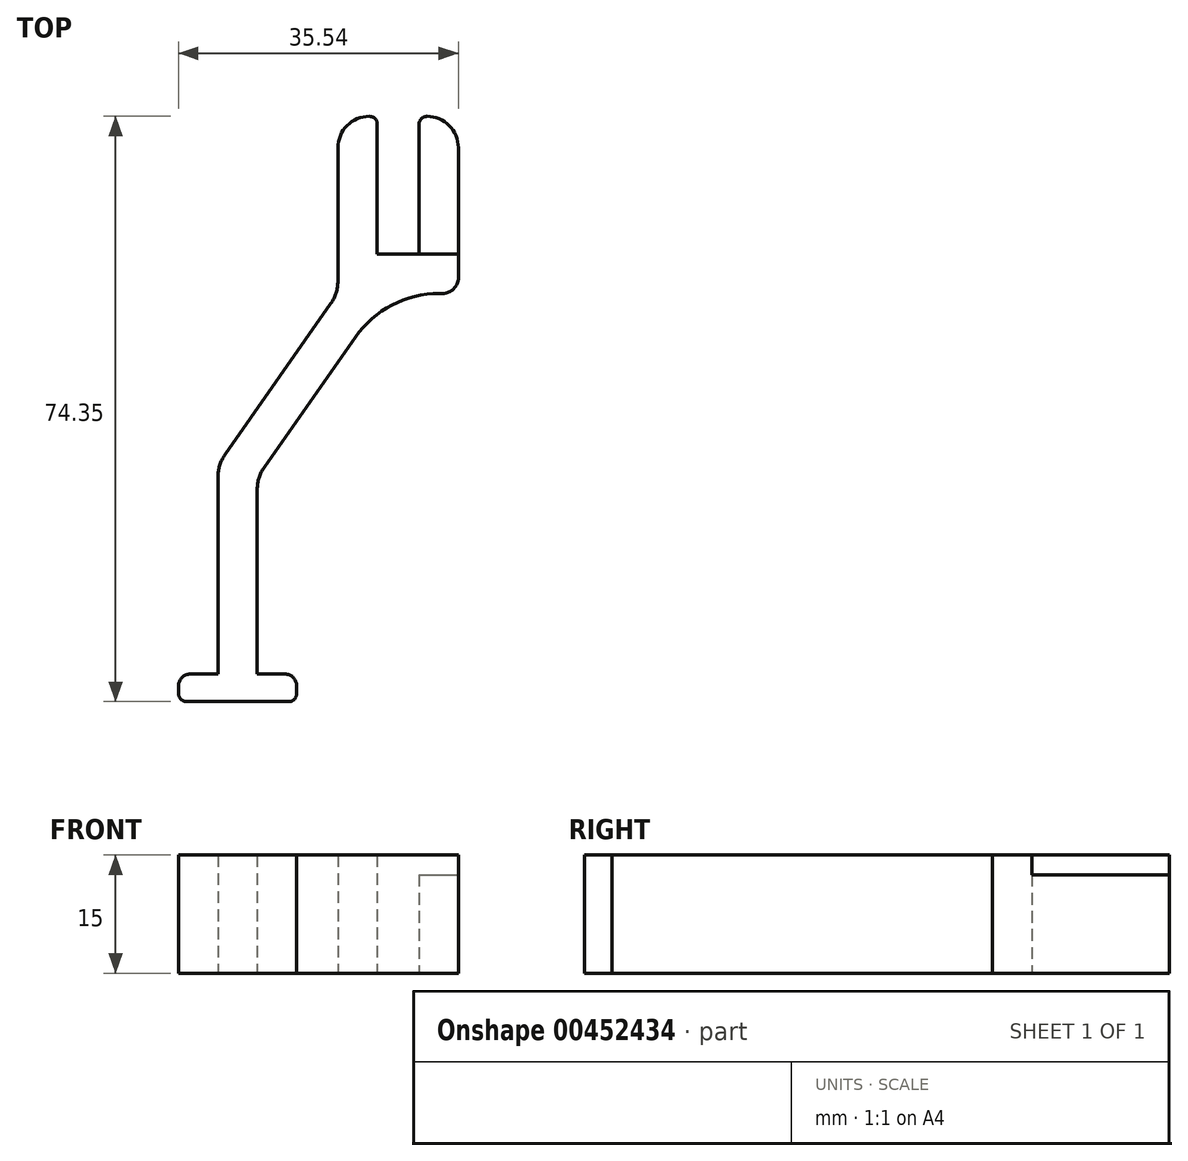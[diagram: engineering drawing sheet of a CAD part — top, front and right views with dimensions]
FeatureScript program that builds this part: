
annotation { "Feature Type Name" : "Feature", "Feature Type Description" : "" }
export const myFeature = defineFeature(function(context is Context, id is Id, definition is map)
    precondition{}
    {
        {
            var Q0;
            Q0=qCreatedBy(makeId("Top.planeOp"),FACE);
            var sketch = newSketch(context, id + "F0", { "sketchPlane" : qUnion([Q0])});
            skLineSegment(sketch, "E0", {"start": v(0, 0) * mm, "end": v(0, 16.5) * mm});
            skLineSegment(sketch, "E1", {"start": v(0, 0) * mm, "end": v(-5.3, 0) * mm});
            skLineSegment(sketch, "E2", {"start": v(-5.3, 0) * mm, "end": v(-5.3, 16.5) * mm});
            skLineSegment(sketch, "E3", {"start": v(1, 17.5) * mm, "end": v(1, 17.5) * mm});
            skLineSegment(sketch, "E4", {"start": v(5, 13.5) * mm, "end": v(5, -3.42) * mm});
            skLineSegment(sketch, "E5", {"start": v(-6.3, 17.5) * mm, "end": v(-6.3, 17.5) * mm});
            skLineSegment(sketch, "E6", {"start": v(-10.3, 13.5) * mm, "end": v(-10.3, -3) * mm});
            skLineSegment(sketch, "E7", {"start": v(5.9, -6.3) * mm, "end": v(19.34, -25.48) * mm});
            skLineSegment(sketch, "E8.0", {"start": v(2.78, -10.54) * mm, "end": v(14.34, -27.06) * mm});
            skLineSegment(sketch, "E9", {"start": v(-8.3, -5) * mm, "end": v(-7.87, -5) * mm});
            skPoint(sketch, "E10.visualSharp", {"position": v(-1.1, -5) * mm});
            skArc(sketch, "E10.filletArc", {"start": v(2.78, -10.54) * mm, "mid": v(-1.87, -6.47) * mm, "end": v(-7.87, -5) * mm});
            skPoint(sketch, "E11.visualSharp", {"position": v(-10.3, 17.5) * mm});
            skArc(sketch, "E11.filletArc", {"start": v(-6.3, 17.5) * mm, "mid": v(-9.13, 16.33) * mm, "end": v(-10.3, 13.5) * mm});
            skPoint(sketch, "E12.visualSharp", {"position": v(-5.3, 17.5) * mm});
            skArc(sketch, "E12.filletArc", {"start": v(-5.3, 16.5) * mm, "mid": v(-5.6, 17.2) * mm, "end": v(-6.3, 17.5) * mm});
            skPoint(sketch, "E13.visualSharp", {"position": v(5, 17.5) * mm});
            skArc(sketch, "E13.filletArc", {"start": v(5, 13.5) * mm, "mid": v(3.83, 16.33) * mm, "end": v(1, 17.5) * mm});
            skPoint(sketch, "E14.visualSharp", {"position": v(0, 17.5) * mm});
            skArc(sketch, "E14.filletArc", {"start": v(1, 17.5) * mm, "mid": v(0.3, 17.2) * mm, "end": v(0, 16.5) * mm});
            skPoint(sketch, "E15.visualSharp", {"position": v(5, -5) * mm});
            skArc(sketch, "E15.filletArc", {"start": v(5, -3.42) * mm, "mid": v(5.23, -4.93) * mm, "end": v(5.9, -6.3) * mm});
            skPoint(sketch, "E16.visualSharp", {"position": v(-10.3, -5) * mm});
            skArc(sketch, "E16.filletArc", {"start": v(-10.3, -3) * mm, "mid": v(-9.71, -4.41) * mm, "end": v(-8.3, -5) * mm});
            skLineSegment(sketch, "E17", {"start": v(15.24, -29.92) * mm, "end": v(15.24, -53.35) * mm});
            skLineSegment(sketch, "E18.0", {"start": v(20.24, -28.35) * mm, "end": v(20.24, -53.35) * mm});
            skPoint(sketch, "E19.visualSharp", {"position": v(20.24, -26.77) * mm});
            skArc(sketch, "E19.filletArc", {"start": v(20.24, -28.35) * mm, "mid": v(20.01, -26.84) * mm, "end": v(19.34, -25.48) * mm});
            skArc(sketch, "E20.filletArc", {"start": v(15.24, -29.92) * mm, "mid": v(15.01, -28.42) * mm, "end": v(14.34, -27.06) * mm});
            skLineSegment(sketch, "E21", {"start": v(20.24, -53.35) * mm, "end": v(23.74, -53.35) * mm});
            skLineSegment(sketch, "E22", {"start": v(15.24, -53.35) * mm, "end": v(11.74, -53.35) * mm});
            skLineSegment(sketch, "E23", {"start": v(10.24, -54.85) * mm, "end": v(10.24, -55.85) * mm});
            skLineSegment(sketch, "E24", {"start": v(25.24, -54.85) * mm, "end": v(25.24, -55.85) * mm});
            skLineSegment(sketch, "E25", {"start": v(24.24, -56.85) * mm, "end": v(11.24, -56.85) * mm});
            skPoint(sketch, "E26.visualSharp", {"position": v(10.24, -53.35) * mm});
            skArc(sketch, "E26.filletArc", {"start": v(11.74, -53.35) * mm, "mid": v(10.68, -53.79) * mm, "end": v(10.24, -54.85) * mm});
            skPoint(sketch, "E27.visualSharp", {"position": v(25.24, -53.35) * mm});
            skArc(sketch, "E27.filletArc", {"start": v(25.24, -54.85) * mm, "mid": v(24.8, -53.79) * mm, "end": v(23.74, -53.35) * mm});
            skPoint(sketch, "E28.visualSharp", {"position": v(25.24, -56.85) * mm});
            skArc(sketch, "E28.filletArc", {"start": v(24.24, -56.85) * mm, "mid": v(24.95, -56.55) * mm, "end": v(25.24, -55.85) * mm});
            skPoint(sketch, "E29.visualSharp", {"position": v(10.24, -56.85) * mm});
            skArc(sketch, "E29.filletArc", {"start": v(10.24, -55.85) * mm, "mid": v(10.54, -56.55) * mm, "end": v(11.24, -56.85) * mm});
            skSolve(sketch);
        }
        {
            var Q0;
            Q0 = qSketchRegion(id + "F0", true);
            extrude(context, id + "F1", {"entities" : qUnion([Q0]), "depth" : 15 * mm, "offsetDistance" : 25 * mm});
        }
        {
            var Q0;
            Q0=makeQuery(id+"F1.opExtrude","SWEPT_BODY",BODY,{"disambiguationData":[OSD([sQuery(id+"F0.wireOp",EDGE,"E0"),sQuery(id+"F0.wireOp",EDGE,"E1"),sQuery(id+"F0.wireOp",EDGE,"E2"),sQuery(id+"F0.wireOp",EDGE,"E4"),sQuery(id+"F0.wireOp",EDGE,"E6"),sQuery(id+"F0.wireOp",EDGE,"E7"),sQuery(id+"F0.wireOp",EDGE,"E8.0"),sQuery(id+"F0.wireOp",EDGE,"E9"),sQuery(id+"F0.wireOp",EDGE,"E10.filletArc"),sQuery(id+"F0.wireOp",EDGE,"E11.filletArc"),sQuery(id+"F0.wireOp",EDGE,"E12.filletArc"),sQuery(id+"F0.wireOp",EDGE,"E13.filletArc"),sQuery(id+"F0.wireOp",EDGE,"E14.filletArc"),sQuery(id+"F0.wireOp",EDGE,"E15.filletArc"),sQuery(id+"F0.wireOp",EDGE,"E16.filletArc"),sQuery(id+"F0.wireOp",EDGE,"E17"),sQuery(id+"F0.wireOp",EDGE,"E18.0"),sQuery(id+"F0.wireOp",EDGE,"E19.filletArc"),sQuery(id+"F0.wireOp",EDGE,"E20.filletArc"),sQuery(id+"F0.wireOp",EDGE,"E21"),sQuery(id+"F0.wireOp",EDGE,"E22"),sQuery(id+"F0.wireOp",EDGE,"E23"),sQuery(id+"F0.wireOp",EDGE,"E24"),sQuery(id+"F0.wireOp",EDGE,"E25"),sQuery(id+"F0.wireOp",EDGE,"E26.filletArc"),sQuery(id+"F0.wireOp",EDGE,"E27.filletArc"),sQuery(id+"F0.wireOp",EDGE,"E28.filletArc"),sQuery(id+"F0.wireOp",EDGE,"E29.filletArc")])]});
            var Q1;
            Q1=makeQuery(id+"F1.opExtrude","SWEPT_FACE",FACE,{"disambiguationData":[OSD([sQuery(id+"F0.wireOp",EDGE,"E6")])]});
            mirror(context, id + "F2", {"entities" : qUnion([Q0]), "mirrorPlane" : qUnion([Q1])});
        }
        {
            var Q0;
            Q0=makeQuery(id+"F1.opExtrude","SWEPT_BODY",BODY,{"disambiguationData":[OSD([sQuery(id+"F0.wireOp",EDGE,"E0"),sQuery(id+"F0.wireOp",EDGE,"E1"),sQuery(id+"F0.wireOp",EDGE,"E2"),sQuery(id+"F0.wireOp",EDGE,"E4"),sQuery(id+"F0.wireOp",EDGE,"E6"),sQuery(id+"F0.wireOp",EDGE,"E7"),sQuery(id+"F0.wireOp",EDGE,"E8.0"),sQuery(id+"F0.wireOp",EDGE,"E9"),sQuery(id+"F0.wireOp",EDGE,"E10.filletArc"),sQuery(id+"F0.wireOp",EDGE,"E11.filletArc"),sQuery(id+"F0.wireOp",EDGE,"E12.filletArc"),sQuery(id+"F0.wireOp",EDGE,"E13.filletArc"),sQuery(id+"F0.wireOp",EDGE,"E14.filletArc"),sQuery(id+"F0.wireOp",EDGE,"E15.filletArc"),sQuery(id+"F0.wireOp",EDGE,"E16.filletArc"),sQuery(id+"F0.wireOp",EDGE,"E17"),sQuery(id+"F0.wireOp",EDGE,"E18.0"),sQuery(id+"F0.wireOp",EDGE,"E19.filletArc"),sQuery(id+"F0.wireOp",EDGE,"E20.filletArc"),sQuery(id+"F0.wireOp",EDGE,"E21"),sQuery(id+"F0.wireOp",EDGE,"E22"),sQuery(id+"F0.wireOp",EDGE,"E23"),sQuery(id+"F0.wireOp",EDGE,"E24"),sQuery(id+"F0.wireOp",EDGE,"E25"),sQuery(id+"F0.wireOp",EDGE,"E26.filletArc"),sQuery(id+"F0.wireOp",EDGE,"E27.filletArc"),sQuery(id+"F0.wireOp",EDGE,"E28.filletArc"),sQuery(id+"F0.wireOp",EDGE,"E29.filletArc")])]});
            deleteBodies(context, id + "F3", {"entities" : qUnion([Q0])});
        }
        {
            var Q0;
            Q0=makeQuery(id+"F2.opPattern","COPY",FACE,{"derivedFrom":makeQuery(id+"F1.opExtrude","SWEPT_FACE",FACE,{"disambiguationData":[OSD([sQuery(id+"F0.wireOp",EDGE,"E6")])]}),"instanceName":"1"});
            var sketch = newSketch(context, id + "F4", { "sketchPlane" : qUnion([Q0])});
            skPoint(sketch, "E30.0", {"position": v(17.5, 15) * mm});
            skPoint(sketch, "E31.0", {"position": v(0, 15) * mm});
            skLineSegment(sketch, "E32", {"start": v(17.5, 15) * mm, "end": v(0, 15) * mm});
            skLineSegment(sketch, "E33", {"start": v(0, 15) * mm, "end": v(0, 12.5) * mm});
            skLineSegment(sketch, "E34", {"start": v(0, 12.5) * mm, "end": v(17.5, 12.5) * mm});
            skLineSegment(sketch, "E35", {"start": v(17.5, 12.5) * mm, "end": v(17.5, 15) * mm});
            skSolve(sketch);
        }
        {
            var Q0;
            Q0 = qSketchRegion(id + "F4", true);
            extrude(context, id + "F5", {"entities" : qUnion([Q0]), "operationType" : NewBodyOperationType.REMOVE, "oppositeDirection" : true, "depth" : 5.7 * mm, "offsetDistance" : 25 * mm});
        }
    });
